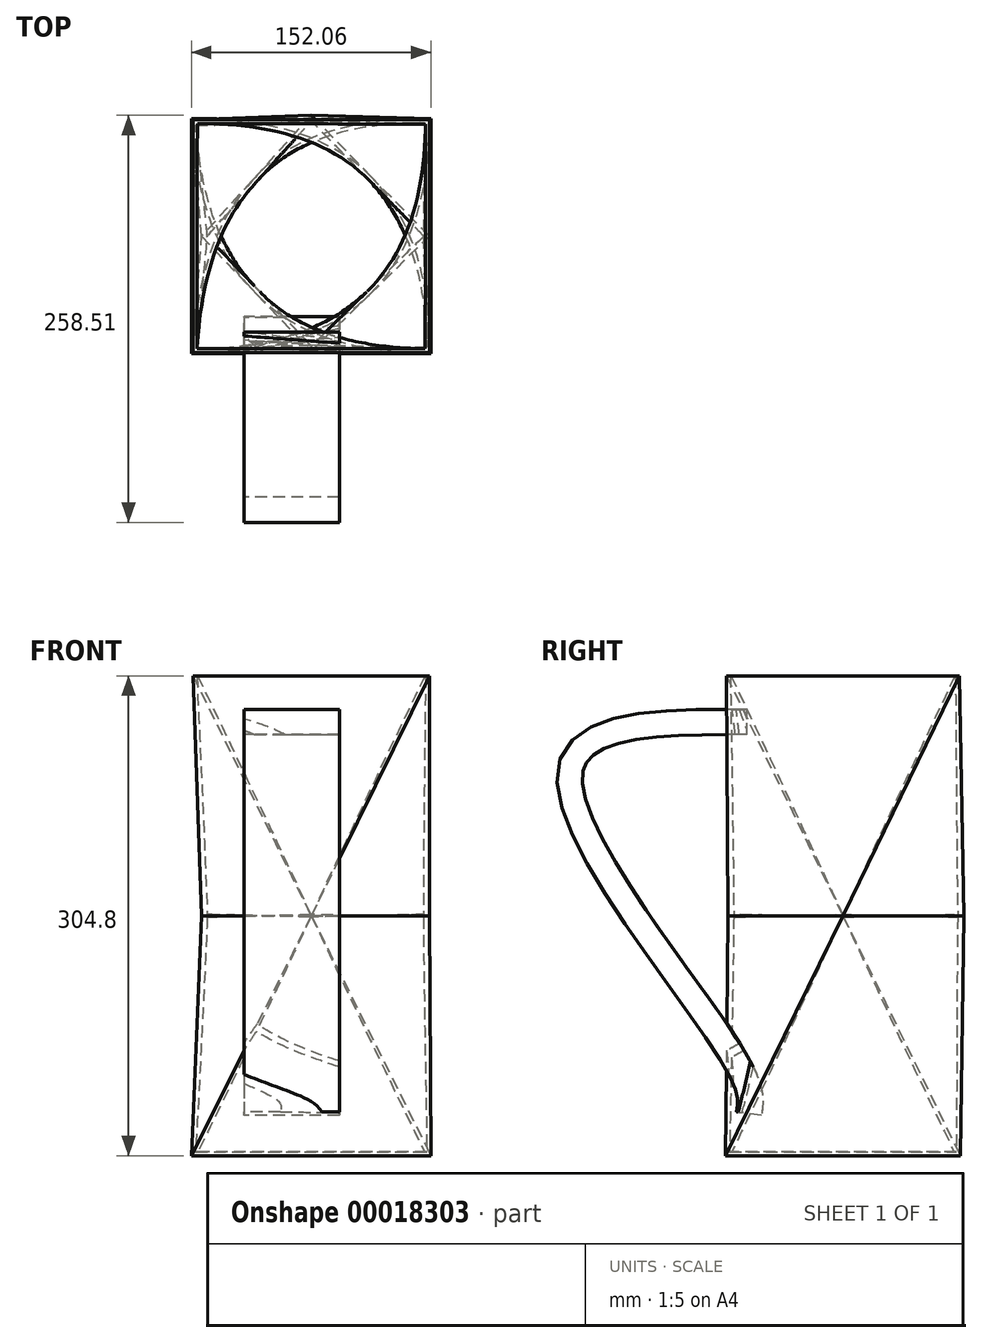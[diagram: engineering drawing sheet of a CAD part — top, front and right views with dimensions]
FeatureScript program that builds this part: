
annotation { "Feature Type Name" : "Feature", "Feature Type Description" : "" }
export const myFeature = defineFeature(function(context is Context, id is Id, definition is map)
    precondition{}
    {
        {
            var Q0;
            Q0=qCreatedBy(makeId("Top.planeOp"),FACE);
            var sketch = newSketch(context, id + "F0", { "sketchPlane" : qUnion([Q0])});
            skLineSegment(sketch, "E0", {"start": v(0, -73.17) * mm, "end": v(74.97, 0) * mm});
            skLineSegment(sketch, "E1", {"start": v(74.97, 0) * mm, "end": v(0, 76.82) * mm});
            skLineSegment(sketch, "E2", {"start": v(0, 76.82) * mm, "end": v(-69.62, 0) * mm});
            skLineSegment(sketch, "E3", {"start": v(-69.62, 0) * mm, "end": v(0, -73.17) * mm});
            skSolve(sketch);
        }
        {
            var Q0;
            Q0=qCreatedBy(makeId("Top.planeOp"),FACE);
            cPlane(context, id + "F1", {"entities" : qUnion([Q0]), "cplaneType" : CPlaneType.OFFSET, "offset" : 152.4 * mm, "width" : 152.4 * mm, "height" : 152.4 * mm});
        }
        {
            var Q0;
            Q0=qCreatedBy(id+"F1.planeOp",FACE);
            var sketch = newSketch(context, id + "F2", { "sketchPlane" : qUnion([Q0])});
            skLineSegment(sketch, "E4.rect.bottom", {"start": v(75.16, 74.01) * mm, "end": v(-75.16, 74.01) * mm});
            skLineSegment(sketch, "E4.rect.top", {"start": v(75.16, -74.01) * mm, "end": v(-75.16, -74.01) * mm});
            skLineSegment(sketch, "E4.rect.left", {"start": v(75.16, 74.01) * mm, "end": v(75.16, -74.01) * mm});
            skLineSegment(sketch, "E4.rect.right", {"start": v(-75.16, 74.01) * mm, "end": v(-75.16, -74.01) * mm});
            skPoint(sketch, "E4.rect.middle", {"position": v(0, 0) * mm});
            skSolve(sketch);
        }
        {
            var Q0;
            Q0=makeQuery(id+"F2.imprint","IMPRINT",FACE,{"disambiguationData":[TD([[makeQuery(id+"F2.imprint","IMPRINT",EDGE,{"derivedFrom":sQuery(id+"F2.wireOp",EDGE,"E4.rect.bottom")}),1.0]])]});
            var Q1;
            Q1=makeQuery(id+"F0.imprint","IMPRINT",FACE,{"disambiguationData":[TD([[makeQuery(id+"F0.imprint","IMPRINT",EDGE,{"derivedFrom":sQuery(id+"F0.wireOp",EDGE,"E0")}),1.0]])]});
            loft(context, id + "F3", {"sheetProfilesArray" : [{ "sheetProfileEntities" : qUnion([Q0]) }, { "sheetProfileEntities" : qUnion([Q1]) }]});
        }
        {
            var Q0;
            Q0=qCreatedBy(makeId("Top.planeOp"),FACE);
            cPlane(context, id + "F4", {"entities" : qUnion([Q0]), "cplaneType" : CPlaneType.OFFSET, "offset" : 152.4 * mm, "oppositeDirection" : true, "width" : 152.4 * mm, "height" : 152.4 * mm});
        }
        {
            var Q0;
            Q0=qCreatedBy(id+"F4.planeOp",FACE);
            var sketch = newSketch(context, id + "F5", { "sketchPlane" : qUnion([Q0])});
            skLineSegment(sketch, "E5.rect.bottom", {"start": v(76.03, -74.57) * mm, "end": v(-76.03, -74.57) * mm});
            skLineSegment(sketch, "E5.rect.top", {"start": v(76.03, 74.57) * mm, "end": v(-76.03, 74.57) * mm});
            skLineSegment(sketch, "E5.rect.left", {"start": v(76.03, -74.57) * mm, "end": v(76.03, 74.57) * mm});
            skLineSegment(sketch, "E5.rect.right", {"start": v(-76.03, -74.57) * mm, "end": v(-76.03, 74.57) * mm});
            skPoint(sketch, "E5.rect.middle", {"position": v(0, 0) * mm});
            skSolve(sketch);
        }
        {
            var Q1;
            Q1=makeQuery(id+"F3.opLoft","CAP_FACE",FACE,{"disambiguationData":[OSD([makeQuery(id+"F0.imprint","IMPRINT",FACE,{"disambiguationData":[TD([[makeQuery(id+"F0.imprint","IMPRINT",EDGE,{"derivedFrom":sQuery(id+"F0.wireOp",EDGE,"E0")}),1.0]])]})])],"isStart":true});
            var Q2;
            Q2=makeQuery(id+"F5.imprint","IMPRINT",FACE,{"disambiguationData":[TD([[makeQuery(id+"F5.imprint","IMPRINT",EDGE,{"derivedFrom":sQuery(id+"F5.wireOp",EDGE,"E5.rect.bottom")}),-1.0]])]});
            loft(context, id + "F6", {"operationType" : NewBodyOperationType.ADD, "sheetProfilesArray" : [{ "sheetProfileEntities" : qUnion([Q1]) }, { "sheetProfileEntities" : qUnion([Q2]) }]});
        }
        {
            var Q0;
            Q0=makeQuery(id+"F3.opLoft","CAP_FACE",FACE,{"disambiguationData":[OSD([makeQuery(id+"F2.imprint","IMPRINT",FACE,{"disambiguationData":[TD([[makeQuery(id+"F2.imprint","IMPRINT",EDGE,{"derivedFrom":sQuery(id+"F2.wireOp",EDGE,"E4.rect.bottom")}),1.0]])]})])],"isStart":true});
            shell(context, id + "F7", {"entities" : qUnion([Q0]), "thickness" : 2.54 * mm});
        }
        {
            var Q0;
            Q0=qCreatedBy(makeId("Front.planeOp"),FACE);
            cPlane(context, id + "F8", {"entities" : qUnion([Q0]), "cplaneType" : CPlaneType.OFFSET, "offset" : 66.04 * mm, "width" : 152.4 * mm, "height" : 152.4 * mm});
        }
        {
            var Q0;
            Q0=qCreatedBy(id+"F8.planeOp",FACE);
            var sketch = newSketch(context, id + "F9", { "sketchPlane" : qUnion([Q0])});
            skLineSegment(sketch, "E6.rect.bottom", {"start": v(17.87, 115.03) * mm, "end": v(-42.74, 115.03) * mm});
            skLineSegment(sketch, "E6.rect.top", {"start": v(17.87, 131.12) * mm, "end": v(-42.74, 131.12) * mm});
            skLineSegment(sketch, "E6.rect.left", {"start": v(17.87, 115.03) * mm, "end": v(17.87, 131.12) * mm});
            skLineSegment(sketch, "E6.rect.right", {"start": v(-42.74, 115.03) * mm, "end": v(-42.74, 131.12) * mm});
            skPoint(sketch, "E6.rect.middle", {"position": v(-12.43, 123.07) * mm});
            skSolve(sketch);
        }
        {
            var Q0;
            Q0=qCreatedBy(makeId("Right.planeOp"),FACE);
            var sketch = newSketch(context, id + "F10", { "sketchPlane" : qUnion([Q0])});
            skFitSpline(sketch, "E7", {"points": [v(-61.03, 121.78) * mm, v(-172.19, 90.49) * mm, v(-64.8, -95.54) * mm, v(-58.38, -125.9) * mm], "startDerivative": vector(-466.02, 0.58) * mm, "endDerivative": vector(-17.94, -120.83) * mm});
            skSolve(sketch);
        }
        {
            var Q0;
            Q0=makeQuery(id+"F9.imprint","IMPRINT",FACE,{"disambiguationData":[TD([[makeQuery(id+"F9.imprint","IMPRINT",EDGE,{"derivedFrom":sQuery(id+"F9.wireOp",EDGE,"E6.rect.bottom")}),-1.0]])]});
            var Q1;
            Q1=sQuery(id+"F10.wireOp",EDGE,"E7");
            sweep(context, id + "F11", {"operationType" : NewBodyOperationType.ADD, "profiles" : qUnion([Q0]), "path" : qUnion([Q1])});
        }
    });
